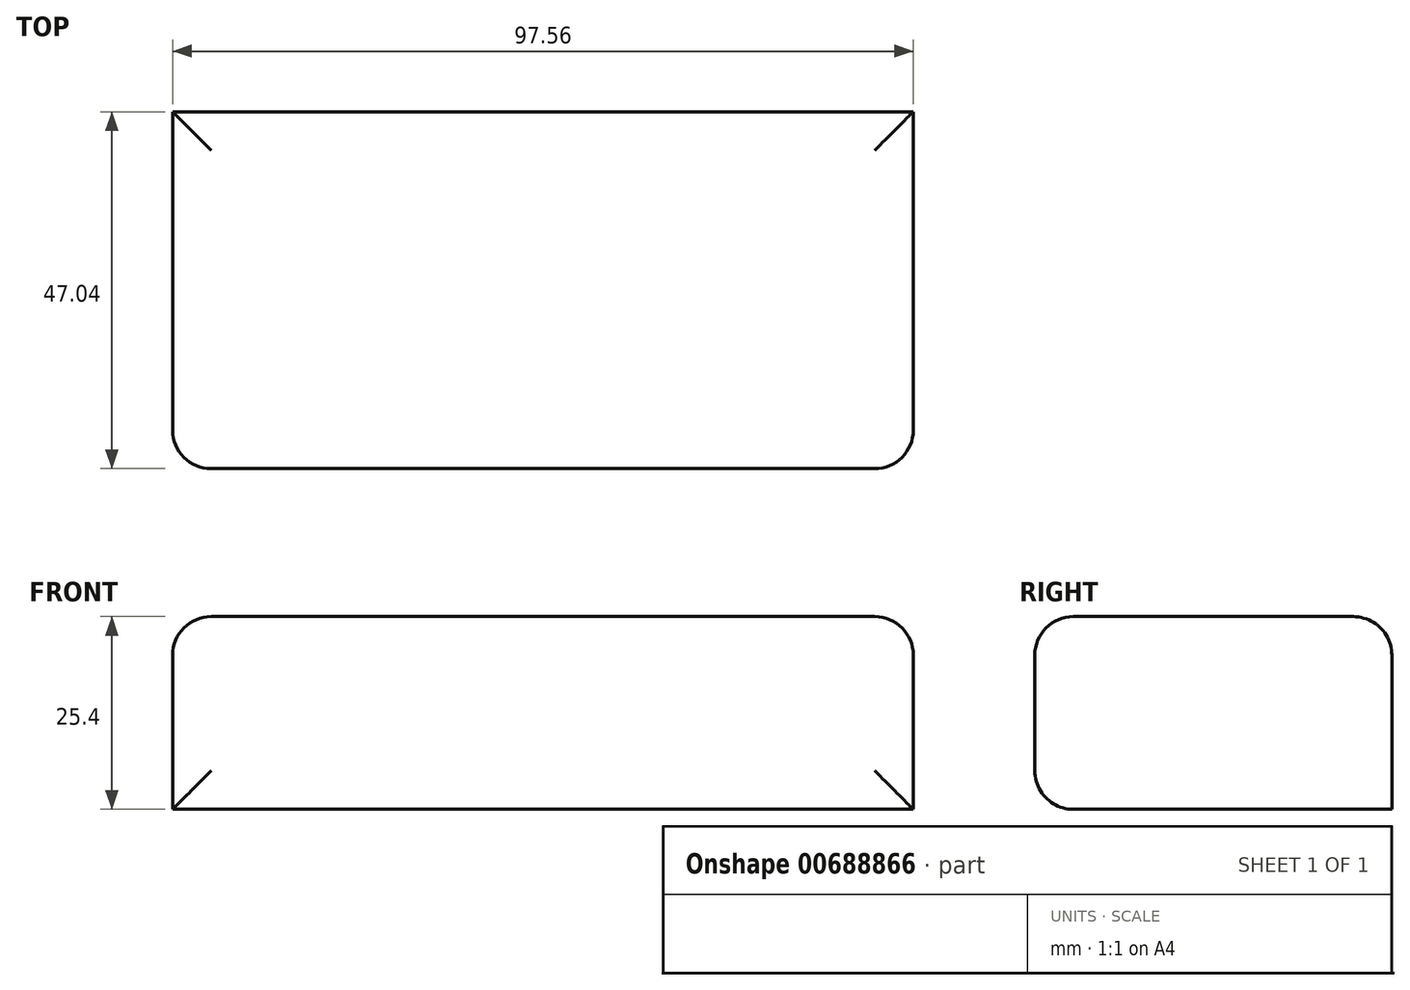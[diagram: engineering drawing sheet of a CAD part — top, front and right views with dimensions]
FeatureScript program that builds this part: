
annotation { "Feature Type Name" : "Feature", "Feature Type Description" : "" }
export const myFeature = defineFeature(function(context is Context, id is Id, definition is map)
    precondition{}
    {
        {
            var Q0;
            Q0=qCreatedBy(makeId("Top.planeOp"),FACE);
            var sketch = newSketch(context, id + "F0", { "sketchPlane" : qUnion([Q0])});
            skLineSegment(sketch, "E0.bottom", {"start": v(73.86, 86.43) * mm, "end": v(-23.7, 86.43) * mm});
            skLineSegment(sketch, "E0.top", {"start": v(73.86, 39.4) * mm, "end": v(-23.7, 39.4) * mm});
            skLineSegment(sketch, "E0.left", {"start": v(73.86, 86.43) * mm, "end": v(73.86, 39.4) * mm});
            skLineSegment(sketch, "E0.right", {"start": v(-23.7, 86.43) * mm, "end": v(-23.7, 39.4) * mm});
            skSolve(sketch);
        }
        {
            var Q0;
            Q0=makeQuery(id+"F0.imprint","IMPRINT",FACE,{"disambiguationData":[TD([[makeQuery(id+"F0.imprint","IMPRINT",EDGE,{"derivedFrom":sQuery(id+"F0.wireOp",EDGE,"E0.bottom")}),1.0]])]});
            var Q1;
            Q1=makeQuery(id+"F0.imprint","IMPRINT",FACE,{"disambiguationData":[TD([[makeQuery(id+"F0.imprint","IMPRINT",EDGE,{"derivedFrom":sQuery(id+"F0.wireOp",EDGE,"E0.bottom")}),1.0]])]});
            extrude(context, id + "F1", {"entities" : qUnion([Q0, Q1]), "depth" : 25.4 * mm, "offsetDistance" : 25.4 * mm});
        }
        {
            var Q0;
            Q0=makeQuery(id+"F1.opExtrude","SWEPT_EDGE",EDGE,{"disambiguationData":[OSD([sQuery(id+"F0.wireOp",EDGE,"E0.top"),sQuery(id+"F0.wireOp",EDGE,"E0.left")])]});
            var Q1;
            Q1=makeQuery(id+"F1.opExtrude","CAP_EDGE",EDGE,{"disambiguationData":[OSD([sQuery(id+"F0.wireOp",EDGE,"E0.top")])],"isStart":false});
            var Q2;
            Q2=makeQuery(id+"F1.opExtrude","SWEPT_EDGE",EDGE,{"disambiguationData":[OSD([sQuery(id+"F0.wireOp",EDGE,"E0.top"),sQuery(id+"F0.wireOp",EDGE,"E0.right")])]});
            var Q3;
            Q3=makeQuery(id+"F1.opExtrude","CAP_EDGE",EDGE,{"disambiguationData":[OSD([sQuery(id+"F0.wireOp",EDGE,"E0.top")])],"isStart":true});
            fillet(context, id + "F2", {"entities" : qUnion([Q0, Q1, Q2, Q3]), "radius" : 5.08 * mm, "tangentPropagation" : true, "allowEdgeOverflow" : false});
        }
        {
            var Q0;
            Q0=makeQuery(id+"F1.opExtrude","SWEPT_FACE",FACE,{"disambiguationData":[OSD([sQuery(id+"F0.wireOp",EDGE,"E0.top")])]});
            var Q1;
            Q1=makeQuery(id+"F1.opExtrude","CAP_FACE",FACE,{"disambiguationData":[OSD([sQuery(id+"F0.wireOp",EDGE,"E0.bottom"),sQuery(id+"F0.wireOp",EDGE,"E0.top"),sQuery(id+"F0.wireOp",EDGE,"E0.left"),sQuery(id+"F0.wireOp",EDGE,"E0.right")])],"isStart":false});
            fillet(context, id + "F3", {"entities" : qUnion([Q0, Q1]), "radius" : 5.08 * mm, "tangentPropagation" : true, "allowEdgeOverflow" : false});
        }
    });
